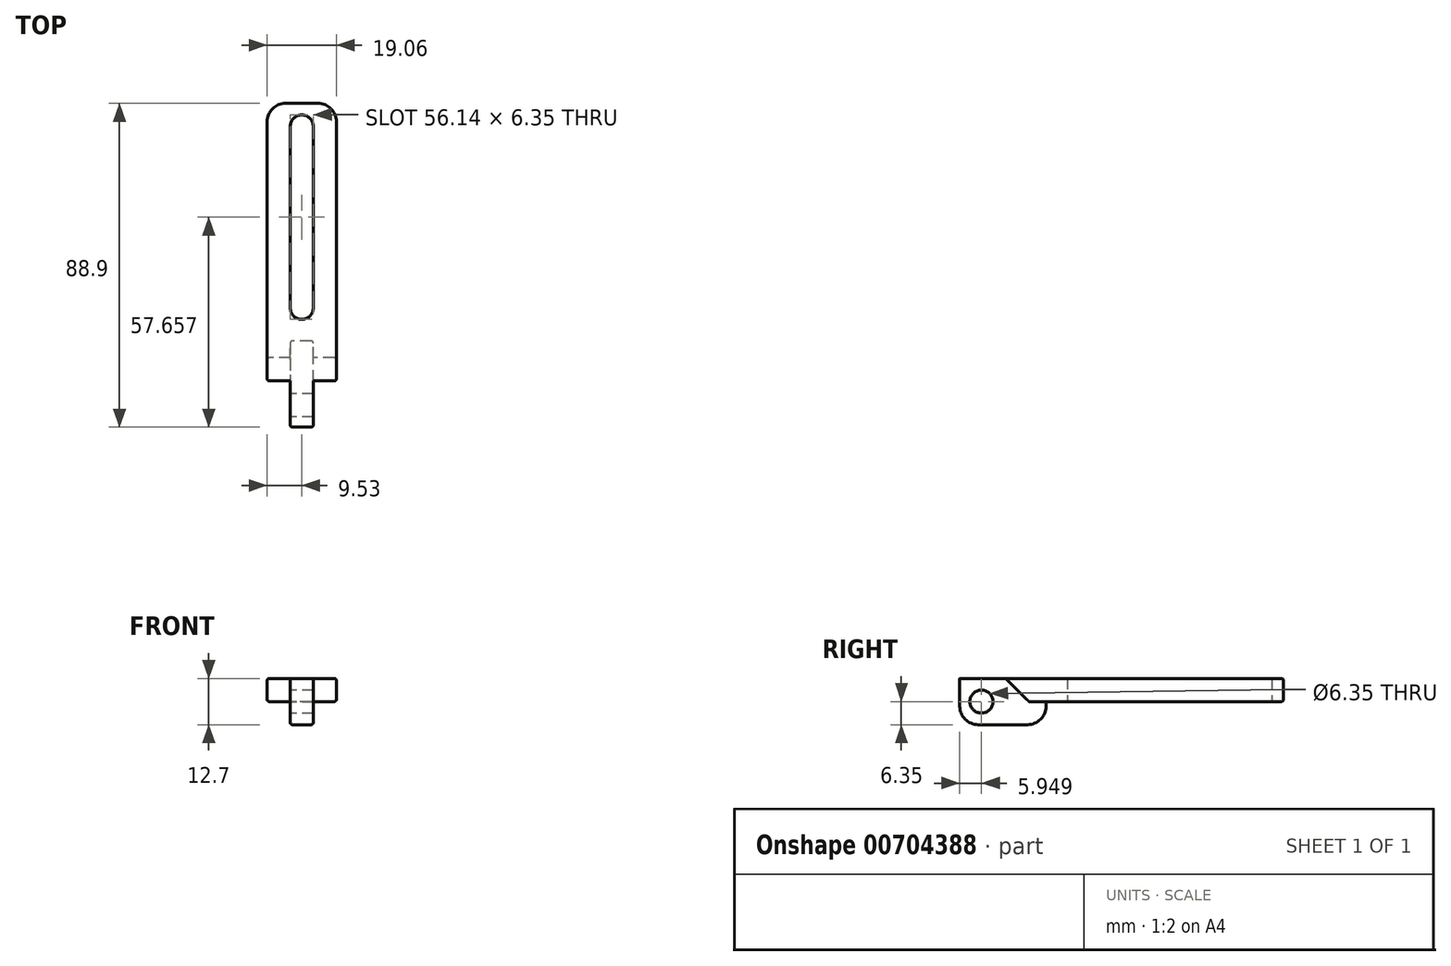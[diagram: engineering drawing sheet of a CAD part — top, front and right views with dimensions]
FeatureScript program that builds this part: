
annotation { "Feature Type Name" : "Feature", "Feature Type Description" : "" }
export const myFeature = defineFeature(function(context is Context, id is Id, definition is map)
    precondition{}
    {
        {
            var Q0;
            Q0=qCreatedBy(makeId("Top.planeOp"),FACE);
            var sketch = newSketch(context, id + "F0", { "sketchPlane" : qUnion([Q0])});
            skLineSegment(sketch, "E0.bottom", {"start": v(-9.52, 38.1) * mm, "end": v(9.53, 38.1) * mm});
            skLineSegment(sketch, "E0.top", {"start": v(-9.53, -38.1) * mm, "end": v(-3.17, -38.1) * mm});
            skLineSegment(sketch, "E0.left", {"start": v(-9.52, 38.1) * mm, "end": v(-9.53, -38.1) * mm});
            skLineSegment(sketch, "E0.right", {"start": v(9.53, 38.1) * mm, "end": v(9.52, -38.1) * mm});
            skPoint(sketch, "E0.middle", {"position": v(0, 0) * mm});
            skLineSegment(sketch, "E1.top", {"start": v(3.18, -50.8) * mm, "end": v(-3.17, -50.8) * mm});
            skLineSegment(sketch, "E1.left", {"start": v(3.18, -38.1) * mm, "end": v(3.18, -50.8) * mm});
            skLineSegment(sketch, "E1.right", {"start": v(-3.17, -38.1) * mm, "end": v(-3.17, -50.8) * mm});
            skPoint(sketch, "E1.middle", {"position": v(0, -38.1) * mm});
            skLineSegment(sketch, "E2.left", {"start": v(-3.17, -18.04) * mm, "end": v(-3.17, 31.75) * mm});
            skLineSegment(sketch, "E2.right", {"start": v(3.18, -18.04) * mm, "end": v(3.17, 31.75) * mm});
            skArc(sketch, "E3", {"start": v(3.18, 31.75) * mm, "mid": v(0, 34.93) * mm, "end": v(-3.18, 31.75) * mm});
            skLineSegment(sketch, "E4.trimOffspring", {"start": v(3.18, -38.1) * mm, "end": v(9.52, -38.1) * mm});
            skPoint(sketch, "E1.bottom.start.orphan", {"position": v(3.18, -25.4) * mm});
            skPoint(sketch, "E5.orphan", {"position": v(-3.17, -25.4) * mm});
            skArc(sketch, "E6", {"start": v(-3.17, -18.04) * mm, "mid": v(0, -21.21) * mm, "end": v(3.17, -18.04) * mm});
            skPoint(sketch, "E7.center.orphan", {"position": v(0, -19.12) * mm});
            skSolve(sketch);
        }
        {
            var Q0;
            Q0=makeQuery(id+"F0.imprint","IMPRINT",FACE,{"disambiguationData":[TD([[makeQuery(id+"F0.imprint","IMPRINT",EDGE,{"derivedFrom":sQuery(id+"F0.wireOp",EDGE,"E0.bottom")}),-1.0]])]});
            var Q1;
            Q1 = qSketchRegion(id + "F2", true);
            extrude(context, id + "F1", {"entities" : qUnion([Q0, Q1]), "depth" : 6.35 * mm, "offsetDistance" : 25.4 * mm});
        }
        {
            var Q0;
            Q0=makeQuery(id+"F1.opExtrude","CAP_FACE",FACE,{"disambiguationData":[OSD([sQuery(id+"F0.wireOp",EDGE,"E0.bottom"),sQuery(id+"F0.wireOp",EDGE,"E0.top"),sQuery(id+"F0.wireOp",EDGE,"E0.left"),sQuery(id+"F0.wireOp",EDGE,"E0.right"),sQuery(id+"F0.wireOp",EDGE,"E1.top"),sQuery(id+"F0.wireOp",EDGE,"E1.left"),sQuery(id+"F0.wireOp",EDGE,"E1.right"),sQuery(id+"F0.wireOp",EDGE,"E2.bottom"),sQuery(id+"F0.wireOp",EDGE,"E2.left"),sQuery(id+"F0.wireOp",EDGE,"E2.right"),sQuery(id+"F0.wireOp",EDGE,"E3"),sQuery(id+"F0.wireOp",EDGE,"E4.trimOffspring")])],"isStart":true});
            var sketch = newSketch(context, id + "F2", { "sketchPlane" : qUnion([Q0])});
            skLineSegment(sketch, "E8.bottom", {"start": v(3.18, 50.8) * mm, "end": v(-3.17, 50.8) * mm});
            skLineSegment(sketch, "E8.left", {"start": v(3.18, 50.8) * mm, "end": v(3.18, 27.13) * mm});
            skLineSegment(sketch, "E8.right", {"start": v(-3.18, 50.8) * mm, "end": v(-3.18, 27.13) * mm});
            skLineSegment(sketch, "E9.bottom", {"start": v(3.18, 50.8) * mm, "end": v(-3.18, 50.8) * mm});
            skLineSegment(sketch, "E9.top", {"start": v(3.18, 27.13) * mm, "end": v(-3.18, 27.13) * mm});
            skSolve(sketch);
        }
        {
            var Q0;
            {var subQ1=sQuery(id+"F2.wireOp",EDGE,"E9.bottom");Q0=makeQuery(id+"F2.imprint","IMPRINT",FACE,{"disambiguationData":[TD([[makeQuery(id+"F2.imprint","IMPRINT",EDGE,{"derivedFrom":subQ1}),1.0]])]});}
            var Q1;
            Q1 = qSketchRegion(id + "F4", true);
            extrude(context, id + "F3", {"entities" : qUnion([Q0, Q1]), "operationType" : NewBodyOperationType.ADD, "depth" : 6.35 * mm, "offsetDistance" : 25.4 * mm});
        }
        {
            var Q0;
            Q0=makeQuery(id+"F3.boolean.opBoolean","MERGE",FACE,{"derivedFrom":[makeQuery(id+"F1.opExtrude","SWEPT_FACE",FACE,{"disambiguationData":[OSD([sQuery(id+"F0.wireOp",EDGE,"E1.right")])]}),makeQuery(id+"F3.opExtrude","SWEPT_FACE",FACE,{"disambiguationData":[OSD([sQuery(id+"F2.wireOp",EDGE,"E8.right")])]})]});
            var sketch = newSketch(context, id + "F4", { "sketchPlane" : qUnion([Q0])});
            skCircle(sketch, "E10", {"center": v(44.85, 0) * mm, "radius": 3.18 * mm});
            skSolve(sketch);
        }
        {
            var Q0;
            Q0=sQuery(id+"F4.wireOp",VERTEX,"E10.center");
            var Q1;
            Q1=makeQuery(id+"F1.opExtrude","SWEPT_BODY",BODY,{"disambiguationData":[OSD([sQuery(id+"F0.wireOp",EDGE,"E0.bottom"),sQuery(id+"F0.wireOp",EDGE,"E0.top"),sQuery(id+"F0.wireOp",EDGE,"E0.left"),sQuery(id+"F0.wireOp",EDGE,"E0.right"),sQuery(id+"F0.wireOp",EDGE,"E1.top"),sQuery(id+"F0.wireOp",EDGE,"E1.left"),sQuery(id+"F0.wireOp",EDGE,"E1.right"),sQuery(id+"F0.wireOp",EDGE,"E2.bottom"),sQuery(id+"F0.wireOp",EDGE,"E2.left"),sQuery(id+"F0.wireOp",EDGE,"E2.right"),sQuery(id+"F0.wireOp",EDGE,"E3"),sQuery(id+"F0.wireOp",EDGE,"E4.trimOffspring")])]});
            hole(context, id + "F5", {"style" : HoleStyle.SIMPLE, "endStyle" : HoleEndStyle.THROUGH, "holeDiameter" : 6.35 * mm, "majorDiameter" : 6.35 * mm, "isTappedThrough" : true, "tappedDepth" : 12.7 * mm, "tapClearance" : 3, "locations" : qUnion([Q0]), "scope" : qUnion([Q1])});
        }
        {
            var Q0;
            Q0=makeQuery(id+"F3.opExtrude","CAP_EDGE",EDGE,{"disambiguationData":[OSD([sQuery(id+"F2.wireOp",EDGE,"E8.bottom")])],"isStart":false});
            var Q1;
            Q1=makeQuery(id+"F3.opExtrude","CAP_EDGE",EDGE,{"disambiguationData":[OSD([sQuery(id+"F2.wireOp",EDGE,"E9.bottom")])],"isStart":false});
            fillet(context, id + "F6", {"entities" : qUnion([Q0, Q1]), "radius" : 5.08 * mm, "tangentPropagation" : true, "allowEdgeOverflow" : false});
        }
        {
            var Q0;
            Q0=makeQuery(id+"F1.opExtrude","SWEPT_EDGE",EDGE,{"disambiguationData":[OSD([sQuery(id+"F0.wireOp",EDGE,"E0.bottom"),sQuery(id+"F0.wireOp",EDGE,"E0.left")])]});
            var Q1;
            Q1=makeQuery(id+"F1.opExtrude","SWEPT_EDGE",EDGE,{"disambiguationData":[OSD([sQuery(id+"F0.wireOp",EDGE,"E0.bottom"),sQuery(id+"F0.wireOp",EDGE,"E0.right")])]});
            fillet(context, id + "F7", {"entities" : qUnion([Q0, Q1]), "radius" : 5.08 * mm, "tangentPropagation" : true, "allowEdgeOverflow" : false});
        }
        {
            var Q0;
            Q0=makeQuery(id+"F1.opExtrude","CAP_EDGE",EDGE,{"disambiguationData":[OSD([sQuery(id+"F0.wireOp",EDGE,"E4.trimOffspring")])],"isStart":true});
            var Q1;
            Q1=makeQuery(id+"F1.opExtrude","CAP_EDGE",EDGE,{"disambiguationData":[OSD([sQuery(id+"F0.wireOp",EDGE,"E0.top")])],"isStart":true});
            chamfer(context, id + "F8", {"entities" : qUnion([Q0, Q1]), "width" : 6.35 * mm, "tangentPropagation" : true});
        }
        {
            var Q0;
            Q0=makeQuery(id+"F3.opExtrude","CAP_EDGE",EDGE,{"disambiguationData":[OSD([sQuery(id+"F2.wireOp",EDGE,"E9.top")])],"isStart":false});
            fillet(context, id + "F9", {"entities" : qUnion([Q0]), "radius" : 5.08 * mm, "tangentPropagation" : true, "allowEdgeOverflow" : false});
        }
        {
            var Q0;
            Q0=makeQuery(id+"F3.boolean.opBoolean","MERGE",EDGE,{"derivedFrom":[makeQuery(id+"F1.opExtrude","SWEPT_EDGE",EDGE,{"disambiguationData":[OSD([sQuery(id+"F0.wireOp",EDGE,"E1.top"),sQuery(id+"F0.wireOp",EDGE,"E1.right")])]}),makeQuery(id+"F3.opExtrude","SWEPT_EDGE",EDGE,{"disambiguationData":[OSD([sQuery(id+"F2.wireOp",EDGE,"E9.bottom"),sQuery(id+"F2.wireOp",EDGE,"E8.right")])]})]});
            var Q1;
            Q1=makeQuery(id+"F3.boolean.opBoolean","MERGE",EDGE,{"derivedFrom":[makeQuery(id+"F1.opExtrude","SWEPT_EDGE",EDGE,{"disambiguationData":[OSD([sQuery(id+"F0.wireOp",EDGE,"E1.top"),sQuery(id+"F0.wireOp",EDGE,"E1.left")])]}),makeQuery(id+"F3.opExtrude","SWEPT_EDGE",EDGE,{"disambiguationData":[OSD([sQuery(id+"F2.wireOp",EDGE,"E9.bottom"),sQuery(id+"F2.wireOp",EDGE,"E8.left")])]})]});
            var Q2;
            Q2=makeQuery(id+"F1.opExtrude","CAP_EDGE",EDGE,{"disambiguationData":[OSD([sQuery(id+"F0.wireOp",EDGE,"E0.left")])],"isStart":true});
            var Q3;
            Q3=makeQuery(id+"F1.opExtrude","CAP_EDGE",EDGE,{"disambiguationData":[OSD([sQuery(id+"F0.wireOp",EDGE,"E0.right")])],"isStart":false});
            fillet(context, id + "F10", {"entities" : qUnion([Q0, Q1, Q2, Q3]), "radius" : 0.64 * mm, "tangentPropagation" : true, "allowEdgeOverflow" : false});
        }
    });
